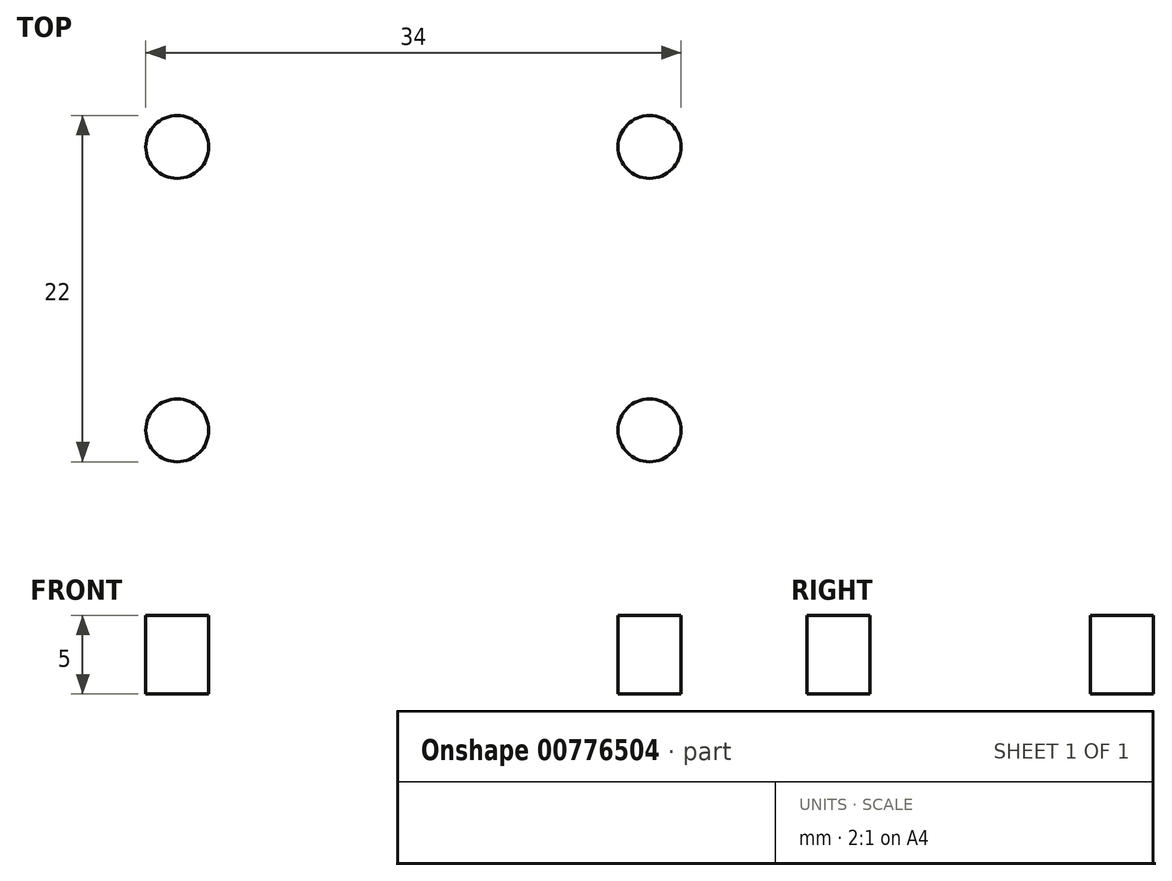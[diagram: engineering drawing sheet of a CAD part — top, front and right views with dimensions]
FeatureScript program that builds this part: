
annotation { "Feature Type Name" : "Feature", "Feature Type Description" : "" }
export const myFeature = defineFeature(function(context is Context, id is Id, definition is map)
    precondition{}
    {
        {
            var Q0;
            Q0=qCreatedBy(makeId("Top.planeOp"),FACE);
            var sketch = newSketch(context, id + "F0", { "sketchPlane" : qUnion([Q0])});
            skLineSegment(sketch, "E0.bottom", {"start": v(0, 0) * mm, "end": v(100, 0) * mm});
            skLineSegment(sketch, "E0.top", {"start": v(0, 150) * mm, "end": v(100, 150) * mm});
            skLineSegment(sketch, "E0.left", {"start": v(0, 0) * mm, "end": v(0, 150) * mm});
            skLineSegment(sketch, "E0.right", {"start": v(100, 0) * mm, "end": v(100, 150) * mm});
            skSolve(sketch);
        }
        {
            var Q0;
            Q0 = qSketchRegion(id + "F0", true);
            extrude(context, id + "F1", {"entities" : qUnion([Q0]), "depth" : 5 * mm, "offsetDistance" : 25 * mm});
        }
        {
            var Q0;
            Q0=makeQuery(id+"F1.opExtrude","CAP_FACE",FACE,{"disambiguationData":[OSD([sQuery(id+"F0.wireOp",EDGE,"E0.bottom"),sQuery(id+"F0.wireOp",EDGE,"E0.top"),sQuery(id+"F0.wireOp",EDGE,"E0.left"),sQuery(id+"F0.wireOp",EDGE,"E0.right")])],"isStart":false});
            var sketch = newSketch(context, id + "F2", { "sketchPlane" : qUnion([Q0])});
            skCircle(sketch, "E1", {"center": v(65, 35) * mm, "radius": 2 * mm});
            skCircle(sketch, "E2", {"center": v(35, 35) * mm, "radius": 2 * mm});
            skCircle(sketch, "E3", {"center": v(65, 53) * mm, "radius": 2 * mm});
            skCircle(sketch, "E4", {"center": v(35, 53) * mm, "radius": 2 * mm});
            skLineSegment(sketch, "E5", {"start": v(-11.17, 75) * mm, "end": v(118.46, 75) * mm, "construction": true});
            skCircle(sketch, "E6.MirrorC", {"center": v(35, 97) * mm, "radius": 2 * mm});
            skCircle(sketch, "E7.MirrorC", {"center": v(65, 97) * mm, "radius": 2 * mm});
            skCircle(sketch, "E8.MirrorC", {"center": v(35, 115) * mm, "radius": 2 * mm});
            skCircle(sketch, "E9.MirrorC", {"center": v(65, 115) * mm, "radius": 2 * mm});
            skSolve(sketch);
        }
        {
            var Q0;
            Q0=makeQuery(id+"F2.imprint","IMPRINT",FACE,{"disambiguationData":[TD([[makeQuery(id+"F2.imprint","IMPRINT",EDGE,{"derivedFrom":sQuery(id+"F2.wireOp",EDGE,"E4")}),1.0]])]});
            var Q1;
            Q1=makeQuery(id+"F2.imprint","IMPRINT",FACE,{"disambiguationData":[TD([[makeQuery(id+"F2.imprint","IMPRINT",EDGE,{"derivedFrom":sQuery(id+"F2.wireOp",EDGE,"E3")}),1.0]])]});
            var Q2;
            Q2=makeQuery(id+"F2.imprint","IMPRINT",FACE,{"disambiguationData":[TD([[makeQuery(id+"F2.imprint","IMPRINT",EDGE,{"derivedFrom":sQuery(id+"F2.wireOp",EDGE,"E2")}),1.0]])]});
            var Q3;
            Q3=makeQuery(id+"F2.imprint","IMPRINT",FACE,{"disambiguationData":[TD([[makeQuery(id+"F2.imprint","IMPRINT",EDGE,{"derivedFrom":sQuery(id+"F2.wireOp",EDGE,"E1")}),1.0]])]});
            var Q4;
            Q4=makeQuery(id+"F2.imprint","IMPRINT",FACE,{"disambiguationData":[TD([[makeQuery(id+"F2.imprint","IMPRINT",EDGE,{"derivedFrom":sQuery(id+"F2.wireOp",EDGE,"E6.MirrorC")}),-1.0]])]});
            var Q5;
            Q5=makeQuery(id+"F2.imprint","IMPRINT",FACE,{"disambiguationData":[TD([[makeQuery(id+"F2.imprint","IMPRINT",EDGE,{"derivedFrom":sQuery(id+"F2.wireOp",EDGE,"E8.MirrorC")}),-1.0]])]});
            var Q6;
            Q6=makeQuery(id+"F2.imprint","IMPRINT",FACE,{"disambiguationData":[TD([[makeQuery(id+"F2.imprint","IMPRINT",EDGE,{"derivedFrom":sQuery(id+"F2.wireOp",EDGE,"E9.MirrorC")}),-1.0]])]});
            var Q7;
            Q7=makeQuery(id+"F2.imprint","IMPRINT",FACE,{"disambiguationData":[TD([[makeQuery(id+"F2.imprint","IMPRINT",EDGE,{"derivedFrom":sQuery(id+"F2.wireOp",EDGE,"E7.MirrorC")}),-1.0]])]});
            extrude(context, id + "F3", {"entities" : qUnion([Q0, Q1, Q2, Q3, Q4, Q5, Q6, Q7]), "operationType" : NewBodyOperationType.REMOVE, "endBound" : BoundingType.THROUGH_ALL, "oppositeDirection" : true, "depth" : 25 * mm, "offsetDistance" : 25 * mm});
        }
    });
